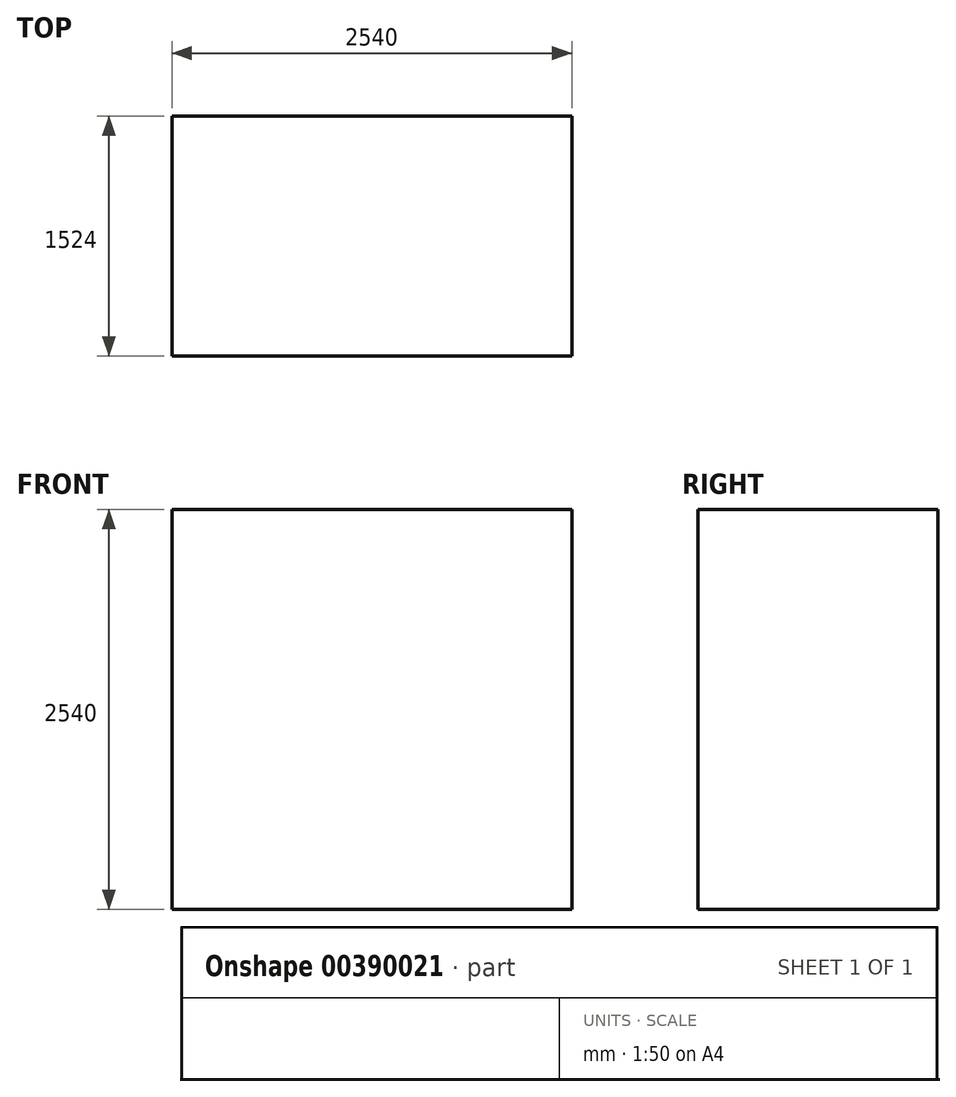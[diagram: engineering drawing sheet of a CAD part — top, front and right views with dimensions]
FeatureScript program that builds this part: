
annotation { "Feature Type Name" : "Feature", "Feature Type Description" : "" }
export const myFeature = defineFeature(function(context is Context, id is Id, definition is map)
    precondition{}
    {
        {
            var Q0;
            Q0=qCreatedBy(makeId("Top.planeOp"),FACE);
            var sketch = newSketch(context, id + "F0", { "sketchPlane" : qUnion([Q0])});
            skLineSegment(sketch, "E0.bottom", {"start": v(1270, 762) * mm, "end": v(-1270, 762) * mm});
            skLineSegment(sketch, "E0.top", {"start": v(1270, -762) * mm, "end": v(-1270, -762) * mm});
            skLineSegment(sketch, "E0.left", {"start": v(1270, 762) * mm, "end": v(1270, -762) * mm});
            skLineSegment(sketch, "E0.right", {"start": v(-1270, 762) * mm, "end": v(-1270, -762) * mm});
            skPoint(sketch, "E0.middle", {"position": v(0, 0) * mm});
            skSolve(sketch);
        }
        {
            var Q0;
            Q0 = qSketchRegion(id + "F0", true);
            extrude(context, id + "F1", {"entities" : qUnion([Q0]), "depth" : 2540 * mm});
        }
    });
